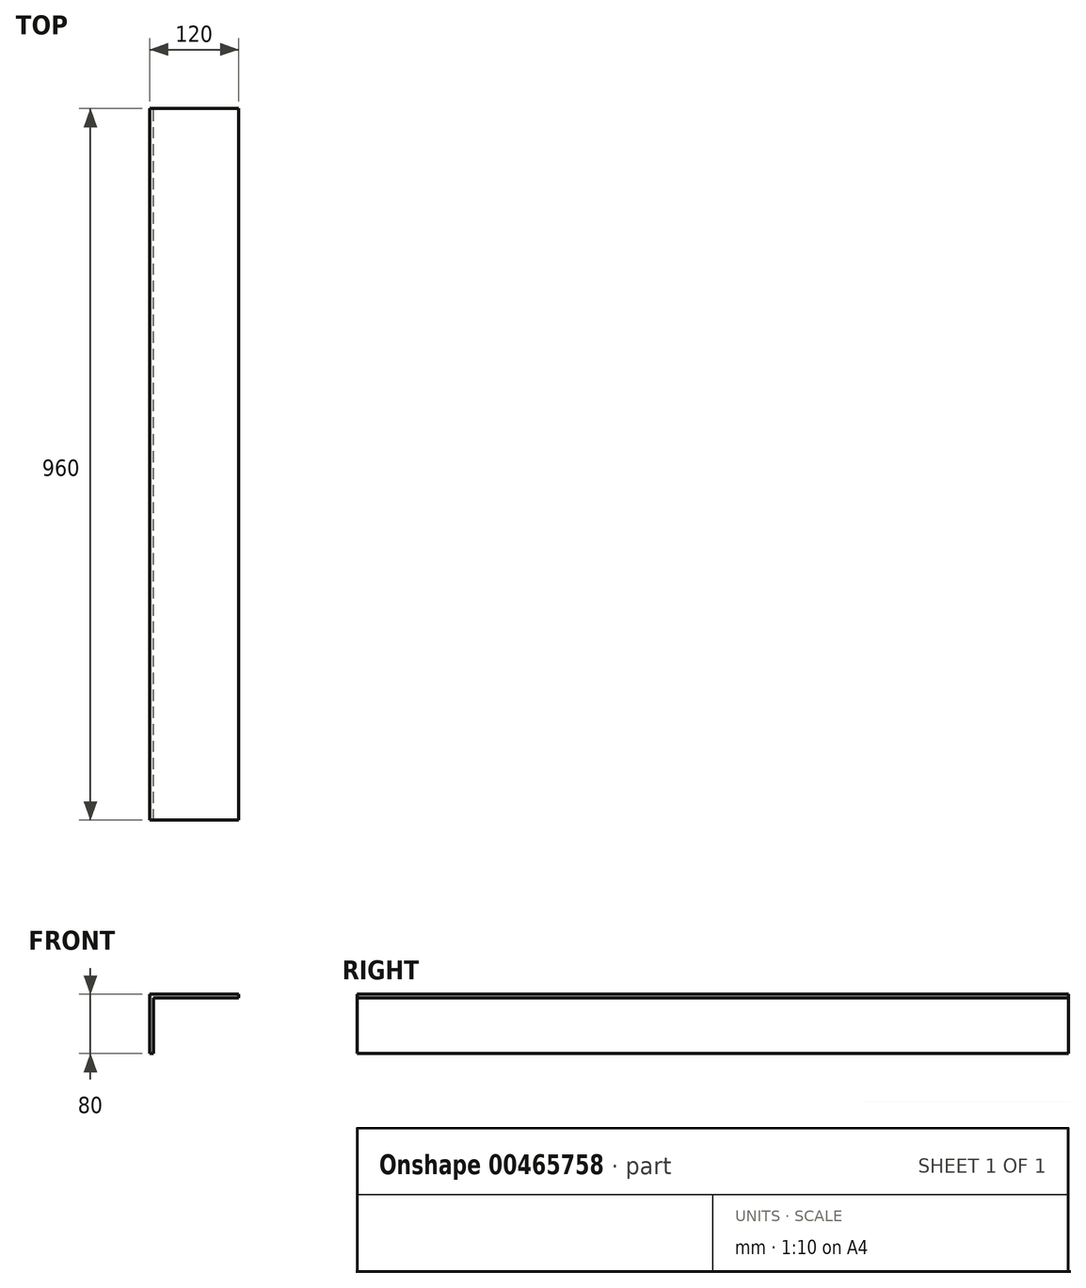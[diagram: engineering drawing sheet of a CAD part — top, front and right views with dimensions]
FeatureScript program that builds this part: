
annotation { "Feature Type Name" : "Feature", "Feature Type Description" : "" }
export const myFeature = defineFeature(function(context is Context, id is Id, definition is map)
    precondition{}
    {
        {
            var Q0;
            Q0=qCreatedBy(makeId("Front.planeOp"),FACE);
            var sketch = newSketch(context, id + "F0", { "sketchPlane" : qUnion([Q0])});
            skLineSegment(sketch, "E0", {"start": v(0, 0) * mm, "end": v(0, 80) * mm});
            skLineSegment(sketch, "E1", {"start": v(0, 80) * mm, "end": v(120, 80) * mm});
            skLineSegment(sketch, "E2", {"start": v(120, 80) * mm, "end": v(120, 75) * mm});
            skLineSegment(sketch, "E3", {"start": v(120, 75) * mm, "end": v(5, 75) * mm});
            skLineSegment(sketch, "E4", {"start": v(5, 75) * mm, "end": v(5, 0) * mm});
            skLineSegment(sketch, "E5", {"start": v(5, 0) * mm, "end": v(0, 0) * mm});
            skSolve(sketch);
        }
        {
            var Q0;
            Q0 = qSketchRegion(id + "F0", true);
            extrude(context, id + "F1", {"entities" : qUnion([Q0]), "depth" : 960 * mm, "offsetDistance" : 25 * mm});
        }
    });
